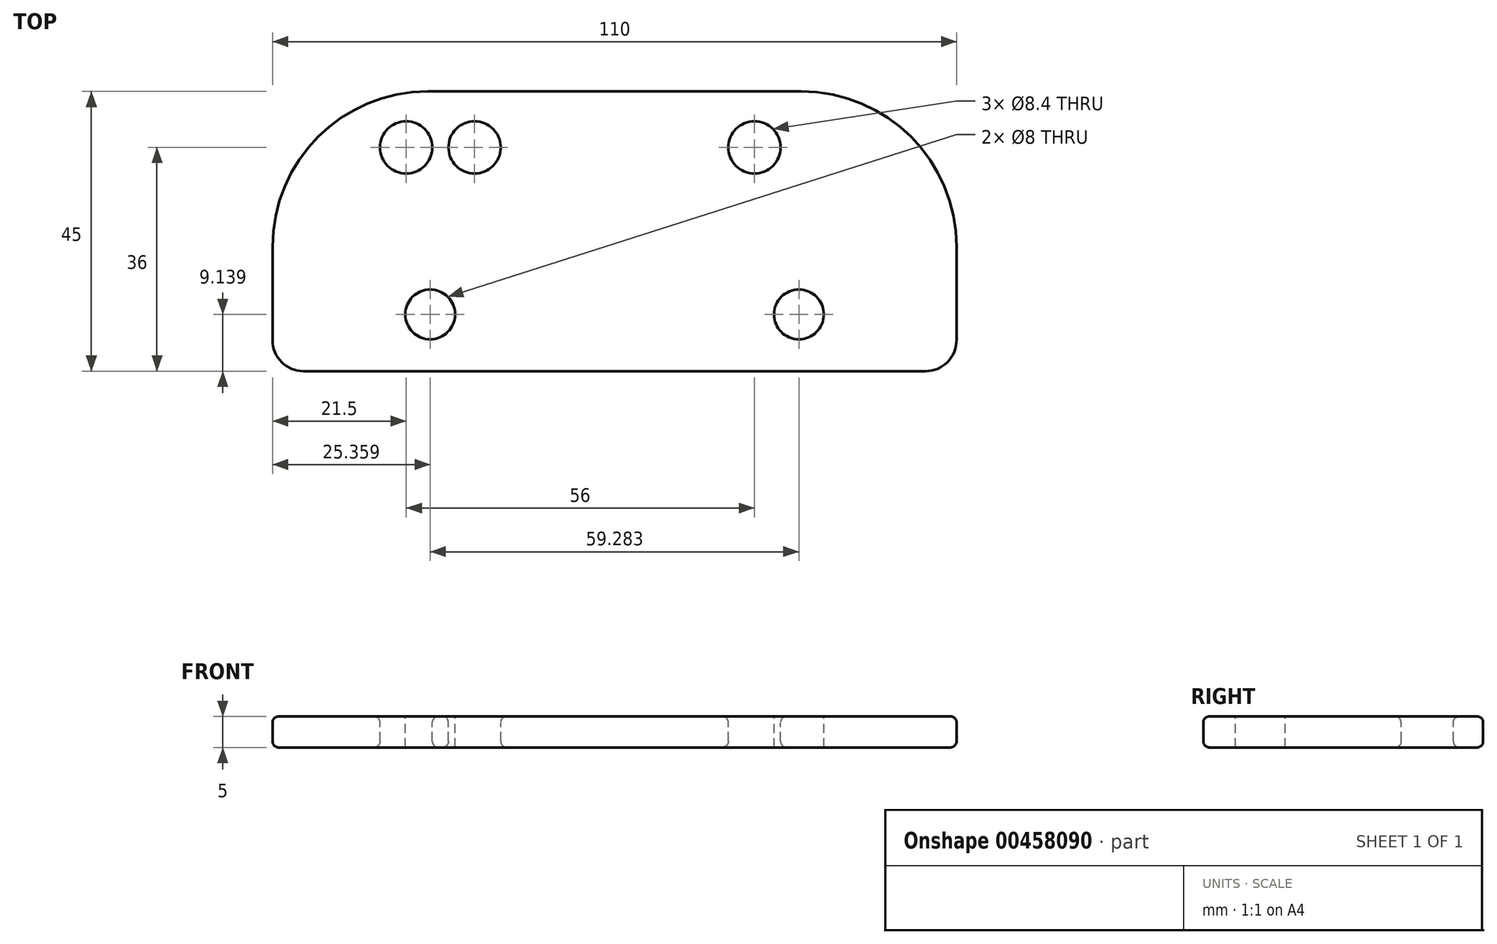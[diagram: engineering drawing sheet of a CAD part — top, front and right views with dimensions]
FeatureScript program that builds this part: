
annotation { "Feature Type Name" : "Feature", "Feature Type Description" : "" }
export const myFeature = defineFeature(function(context is Context, id is Id, definition is map)
    precondition{}
    {
        {
            var Q0;
            Q0=qCreatedBy(makeId("Top.planeOp"),FACE);
            var sketch = newSketch(context, id + "F0", { "sketchPlane" : qUnion([Q0])});
            skLineSegment(sketch, "E0.bottom", {"start": v(-30, 22.5) * mm, "end": v(30, 22.5) * mm});
            skLineSegment(sketch, "E0.top", {"start": v(-55, -22.5) * mm, "end": v(55, -22.5) * mm});
            skLineSegment(sketch, "E0.left", {"start": v(-55, -2.5) * mm, "end": v(-55, -22.5) * mm});
            skLineSegment(sketch, "E0.right", {"start": v(55, -2.5) * mm, "end": v(55, -22.5) * mm});
            skPoint(sketch, "E0.middle", {"position": v(0, 0) * mm});
            skCircle(sketch, "E1", {"center": v(22.5, 13.5) * mm, "radius": 25 * mm, "construction": true});
            skLineSegment(sketch, "E2", {"start": v(0, -2.6) * mm, "end": v(0, 84.85) * mm, "construction": true});
            skCircle(sketch, "E3.MirrorC", {"center": v(-22.5, 13.5) * mm, "radius": 25 * mm, "construction": true});
            skCircle(sketch, "E4", {"center": v(-22.5, 13.5) * mm, "radius": 4.2 * mm});
            skCircle(sketch, "E5.MirrorC", {"center": v(22.5, 13.5) * mm, "radius": 4.2 * mm});
            skPoint(sketch, "E6.visualSharp", {"position": v(-55, 22.5) * mm});
            skArc(sketch, "E6.filletArc", {"start": v(-30, 22.5) * mm, "mid": v(-47.68, 15.18) * mm, "end": v(-55, -2.5) * mm});
            skPoint(sketch, "E7.visualSharp", {"position": v(55, 22.5) * mm});
            skArc(sketch, "E7.filletArc", {"start": v(55, -2.5) * mm, "mid": v(47.68, 15.18) * mm, "end": v(30, 22.5) * mm});
            skLineSegment(sketch, "E8", {"start": v(22.5, 13.5) * mm, "end": v(-112.32, 13.5) * mm, "construction": true});
            skCircle(sketch, "E9", {"center": v(-33.5, 13.5) * mm, "radius": 4.2 * mm});
            skCircle(sketch, "E10", {"center": v(-33.5, 13.5) * mm, "radius": 25 * mm, "construction": true});
            skSolve(sketch);
        }
        {
            var Q0;
            Q0=qSketchRegion(id+"F0",true);
            extrude(context, id + "F1", {"entities" : qUnion([Q0]), "oppositeDirection" : true, "depth" : 5 * mm});
        }
        {
            var Q0;
            Q0=makeQuery(id+"F1.opExtrude","SWEPT_EDGE",EDGE,{"disambiguationData":[OSD([sQuery(id+"F0.wireOp",EDGE,"E0.top"),sQuery(id+"F0.wireOp",EDGE,"E0.right")])]});
            var Q1;
            Q1=makeQuery(id+"F1.opExtrude","SWEPT_EDGE",EDGE,{"disambiguationData":[OSD([sQuery(id+"F0.wireOp",EDGE,"E0.top"),sQuery(id+"F0.wireOp",EDGE,"E0.left")])]});
            fillet(context, id + "F2", {"entities" : qUnion([Q0, Q1]), "radius" : 5 * mm, "tangentPropagation" : true, "allowEdgeOverflow" : false});
        }
        {
            var Q0;
            Q0=makeQuery(id+"F1.opExtrude","CAP_FACE",FACE,{"disambiguationData":[OSD([sQuery(id+"F0.wireOp",EDGE,"E0.bottom"),sQuery(id+"F0.wireOp",EDGE,"E0.top"),sQuery(id+"F0.wireOp",EDGE,"E0.left"),sQuery(id+"F0.wireOp",EDGE,"E0.right"),sQuery(id+"F0.wireOp",EDGE,"E4"),sQuery(id+"F0.wireOp",EDGE,"E5.MirrorC"),sQuery(id+"F0.wireOp",EDGE,"E6.filletArc"),sQuery(id+"F0.wireOp",EDGE,"E7.filletArc")])],"isStart":true});
            var Q1;
            Q1=makeQuery(id+"F1.opExtrude","CAP_FACE",FACE,{"disambiguationData":[OSD([sQuery(id+"F0.wireOp",EDGE,"E0.bottom"),sQuery(id+"F0.wireOp",EDGE,"E0.top"),sQuery(id+"F0.wireOp",EDGE,"E0.left"),sQuery(id+"F0.wireOp",EDGE,"E0.right"),sQuery(id+"F0.wireOp",EDGE,"E4"),sQuery(id+"F0.wireOp",EDGE,"E5.MirrorC"),sQuery(id+"F0.wireOp",EDGE,"E6.filletArc"),sQuery(id+"F0.wireOp",EDGE,"E7.filletArc")])],"isStart":false});
            fillet(context, id + "F3", {"entities" : qUnion([Q0, Q1]), "radius" : 1 * mm, "tangentPropagation" : true, "allowEdgeOverflow" : false});
        }
        {
            var Q0;
            Q0=makeQuery(id+"F1.opExtrude","CAP_FACE",FACE,{"disambiguationData":[OSD([sQuery(id+"F0.wireOp",EDGE,"E0.bottom"),sQuery(id+"F0.wireOp",EDGE,"E0.top"),sQuery(id+"F0.wireOp",EDGE,"E0.left"),sQuery(id+"F0.wireOp",EDGE,"E0.right"),sQuery(id+"F0.wireOp",EDGE,"E4"),sQuery(id+"F0.wireOp",EDGE,"E5.MirrorC"),sQuery(id+"F0.wireOp",EDGE,"E6.filletArc"),sQuery(id+"F0.wireOp",EDGE,"E7.filletArc")])],"isStart":true});
            var sketch = newSketch(context, id + "F4", { "sketchPlane" : qUnion([Q0])});
            skCircle(sketch, "E11", {"center": v(29.64, -13.36) * mm, "radius": 4 * mm});
            skLineSegment(sketch, "E12", {"start": v(-1.39, 0) * mm, "end": v(-1.17, -1.75) * mm, "construction": true});
            skCircle(sketch, "E13.MirrorC", {"center": v(-29.64, -13.36) * mm, "radius": 4 * mm});
            skSolve(sketch);
        }
        {
            var Q0;
            Q0=qSketchRegion(id+"F4",true);
            extrude(context, id + "F5", {"entities" : qUnion([Q0]), "operationType" : NewBodyOperationType.REMOVE, "endBound" : BoundingType.THROUGH_ALL, "oppositeDirection" : true, "depth" : 25 * mm});
        }
    });
